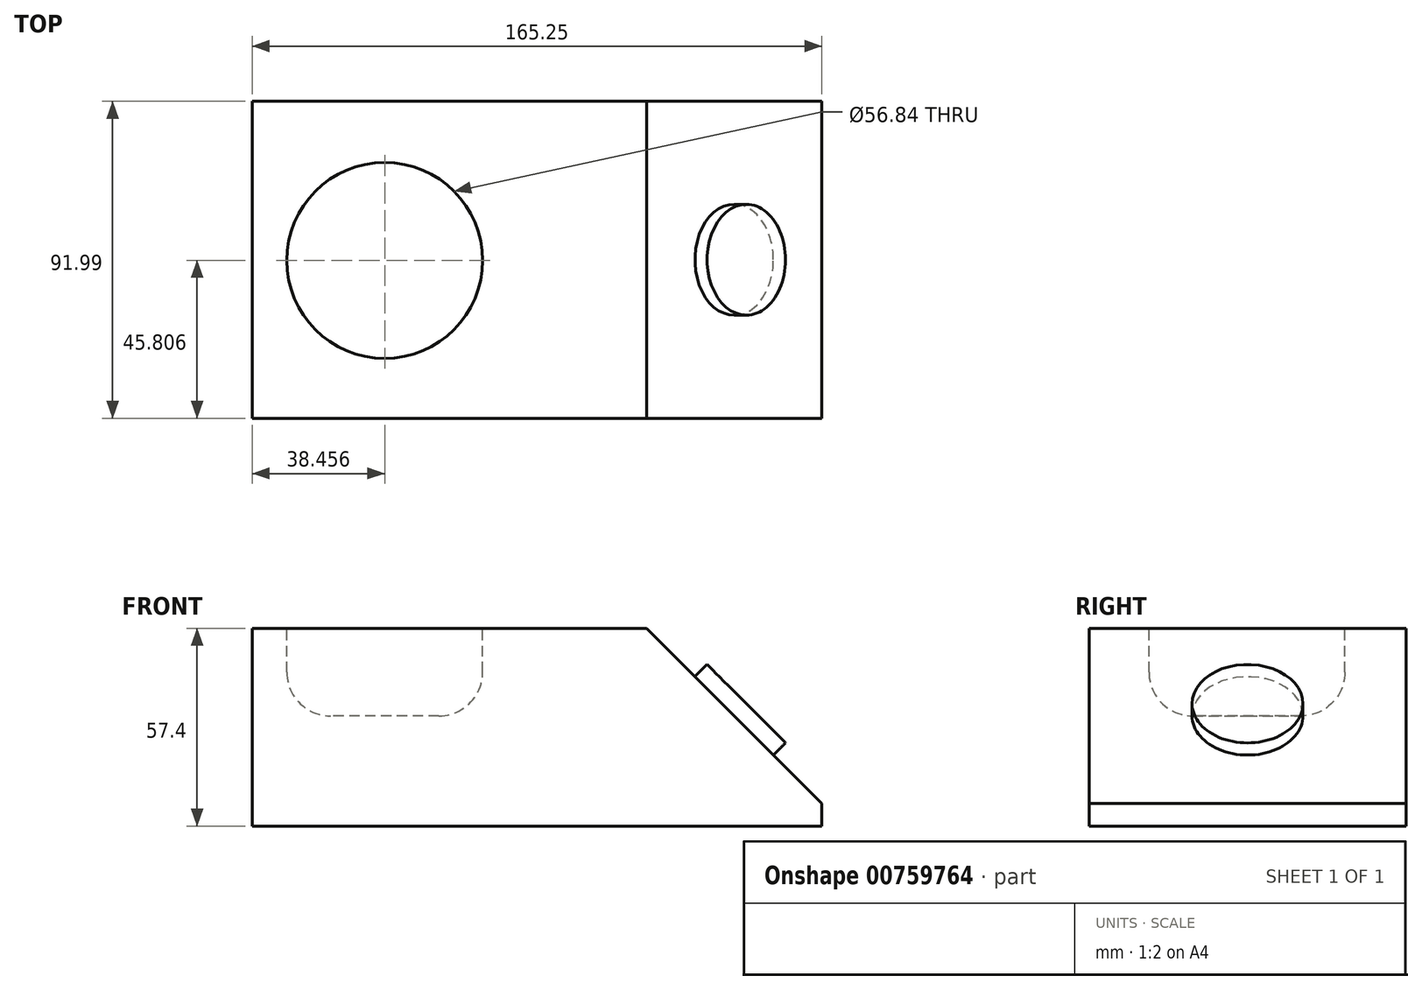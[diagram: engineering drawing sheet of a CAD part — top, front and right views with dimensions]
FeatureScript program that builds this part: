
annotation { "Feature Type Name" : "Feature", "Feature Type Description" : "" }
export const myFeature = defineFeature(function(context is Context, id is Id, definition is map)
    precondition{}
    {
        {
            var Q0;
            Q0=qCreatedBy(makeId("Top.planeOp"),FACE);
            var sketch = newSketch(context, id + "F0", { "sketchPlane" : qUnion([Q0])});
            skLineSegment(sketch, "E0.bottom", {"start": v(-126.41, 55.03) * mm, "end": v(38.84, 55.03) * mm});
            skLineSegment(sketch, "E0.top", {"start": v(-126.41, -36.96) * mm, "end": v(38.84, -36.96) * mm});
            skLineSegment(sketch, "E0.left", {"start": v(-126.41, 55.03) * mm, "end": v(-126.41, -36.96) * mm});
            skLineSegment(sketch, "E0.right", {"start": v(38.84, 55.03) * mm, "end": v(38.84, -36.96) * mm});
            skSolve(sketch);
        }
        {
            var Q0;
            Q0=makeQuery(id+"F0.imprint","IMPRINT",FACE,{"disambiguationData":[TD([[makeQuery(id+"F0.imprint","IMPRINT",EDGE,{"derivedFrom":sQuery(id+"F0.wireOp",EDGE,"E0.bottom")}),-1.0]])]});
            extrude(context, id + "F1", {"entities" : qUnion([Q0]), "depth" : 57.4 * mm, "offsetDistance" : 25.4 * mm});
        }
        {
            var Q0;
            Q0=makeQuery(id+"F1.opExtrude","CAP_FACE",FACE,{"disambiguationData":[OSD([sQuery(id+"F0.wireOp",EDGE,"E0.bottom"),sQuery(id+"F0.wireOp",EDGE,"E0.top"),sQuery(id+"F0.wireOp",EDGE,"E0.left"),sQuery(id+"F0.wireOp",EDGE,"E0.right")])],"isStart":false});
            var sketch = newSketch(context, id + "F2", { "sketchPlane" : qUnion([Q0])});
            skCircle(sketch, "E1", {"center": v(-87.95, 8.85) * mm, "radius": 28.42 * mm});
            skSolve(sketch);
        }
        {
            var Q0;
            Q0=makeQuery(id+"F2.imprint","IMPRINT",FACE,{"disambiguationData":[TD([[makeQuery(id+"F2.imprint","IMPRINT",EDGE,{"derivedFrom":sQuery(id+"F2.wireOp",EDGE,"E1")}),1.0]])]});
            extrude(context, id + "F3", {"entities" : qUnion([Q0]), "operationType" : NewBodyOperationType.REMOVE, "oppositeDirection" : true, "depth" : 25.4 * mm, "offsetDistance" : 25.4 * mm});
        }
        {
            var Q0;
            Q0=makeQuery(id+"F3.boolean.opBoolean","COPY",EDGE,{"derivedFrom":makeQuery(id+"F3.opExtrude","CAP_EDGE",EDGE,{"disambiguationData":[OSD([sQuery(id+"F2.wireOp",EDGE,"E1")])],"isStart":true})});
            var Q1;
            Q1=makeQuery(id+"F3.boolean.opBoolean","COPY",EDGE,{"derivedFrom":makeQuery(id+"F3.opExtrude","CAP_EDGE",EDGE,{"disambiguationData":[OSD([sQuery(id+"F2.wireOp",EDGE,"E1")])],"isStart":false})});
            fillet(context, id + "F4", {"entities" : qUnion([Q0, Q1]), "radius" : 12.7 * mm, "tangentPropagation" : true, "allowEdgeOverflow" : false});
        }
        {
            var Q0;
            Q0=makeQuery(id+"F1.opExtrude","CAP_EDGE",EDGE,{"disambiguationData":[OSD([sQuery(id+"F0.wireOp",EDGE,"E0.right")])],"isStart":false});
            chamfer(context, id + "F5", {"entities" : qUnion([Q0]), "width" : 50.8 * mm, "tangentPropagation" : true});
        }
        {
            var Q0;
            Q0=makeQuery(id+"F5.opChamfer","BLEND_FACE",FACE,{"disambiguationData":[OSD([sQuery(id+"F0.wireOp",EDGE,"E0.right")])]});
            var sketch = newSketch(context, id + "F6", { "sketchPlane" : qUnion([Q0])});
            skCircle(sketch, "E2", {"center": v(9.04, 13.13) * mm, "radius": 16.08 * mm});
            skPoint(sketch, "E2.centerSnap0", {"position": v(9.04, -22.8) * mm});
            skPoint(sketch, "E2.centerSnap1", {"position": v(-36.96, 13.13) * mm});
            skSolve(sketch);
        }
        {
            var Q0;
            Q0=makeQuery(id+"F6.imprint","IMPRINT",FACE,{"disambiguationData":[TD([[makeQuery(id+"F6.imprint","IMPRINT",EDGE,{"derivedFrom":sQuery(id+"F6.wireOp",EDGE,"E2")}),1.0]])]});
            extrude(context, id + "F7", {"entities" : qUnion([Q0]), "operationType" : NewBodyOperationType.ADD, "depth" : 5 * mm, "offsetDistance" : 25 * mm});
        }
    });
